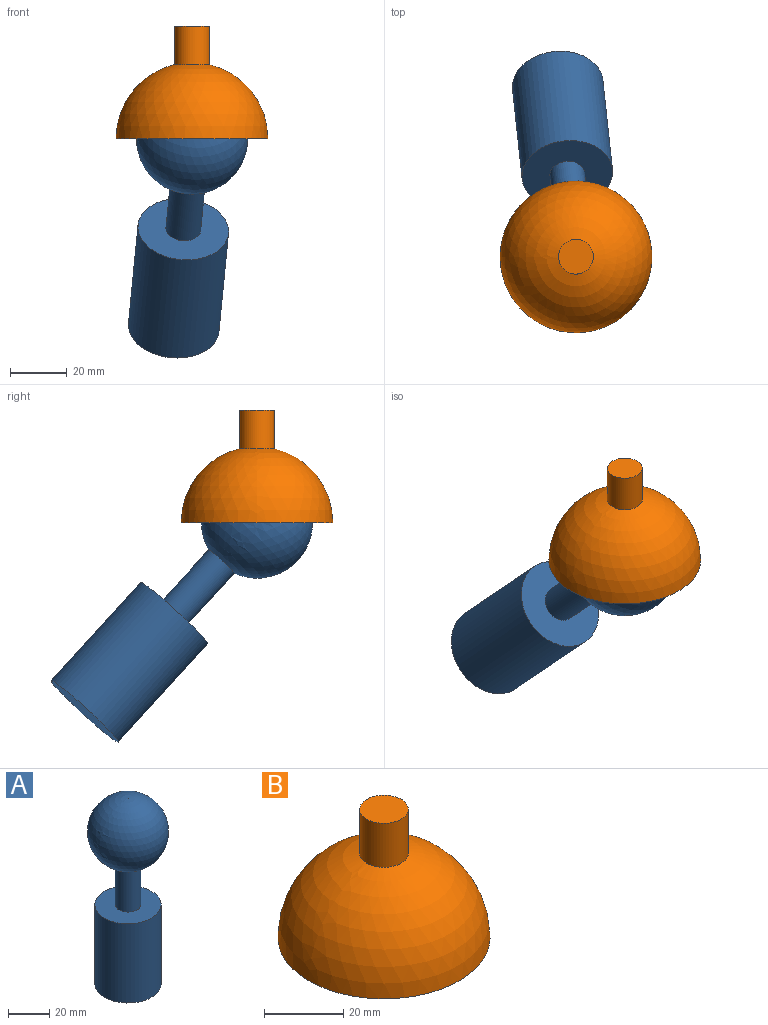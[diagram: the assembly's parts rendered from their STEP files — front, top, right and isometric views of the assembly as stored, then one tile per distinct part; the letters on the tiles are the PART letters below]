
ASSEMBLY  parts=2 mates=1
PART A: 5 faces, bbox 39.2x39.2x109.7 mm
  f0: plane 31.97x31.97mm, normal (0,0,-1), area 802.9mm2, adj f1
  f1: cylinder r=15.99mm len=46.83mm, axis (0,0,-1), area 4703.8mm2, adj f0,f2
  f2: plane 31.97x31.97mm, normal (0,0,1), area 685.1mm2, adj f1,f3
  f3: cylinder r=6.12mm len=24.69mm, axis (0,0,-1), area 949.9mm2, adj f2,f4
  f4: sphere r=19.6mm, area 4704.9mm2, adj f3
PART B: 5 faces, bbox 53.4x53.4x39.6 mm
  f0: sphere r=19.6mm, area 2412.9mm2, adj f1
  f1: plane 53.42x53.42mm, normal (0,0,-1), area 1034.6mm2, adj f0,f2
  f2: sphere r=26.71mm, area 4362.7mm2, adj f1,f3
  f3: cylinder r=6.12mm len=13.6mm, axis (0,0,-1), area 523.1mm2, adj f2,f4
  f4: plane 12.25x12.25mm, normal (0,0,1), area 117.8mm2, adj f3
PLACE A rot(axis=(0.99,0.07,0.09),42.7deg) t=(-1.62,15.22,5.96)mm
PLACE B at identity fixed
MATE ball B.f3 <-> A.f1  axis (0,0,-1) through (0,0,22.63)mm
